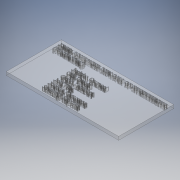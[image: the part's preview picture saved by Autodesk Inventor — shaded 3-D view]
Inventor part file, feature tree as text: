
AUTODESK INVENTOR PART (.ipt)
format: ipt  version: 2018 (Build 220112000, 112)  size: 2,596,864 bytes
history: native  units: mm
features: extrude x2, sketch x2
ambient origin geometry x8: Origin, YZ Plane, XZ Plane, XY Plane, X Axis, Y Axis, Z Axis, Center Point
bodies: Solid1 (feature_tree)
feature tree (4):
  extrude  "Extrusion1"  Depth=49.027mm
  extrude  "Extrusion2"  Depth=3.0mm TaperAngle=0.0deg
  sketch  "Sketch1"  dims[d0=100.0mm d1=49.027mm]
  sketch  "Sketch2"  dims[d2=3.0mm d3=0.0mm d4=3.0mm d5=0.0mm d12=95.0mm d14=45.0mm d15=27.5mm d16=2.5mm]
